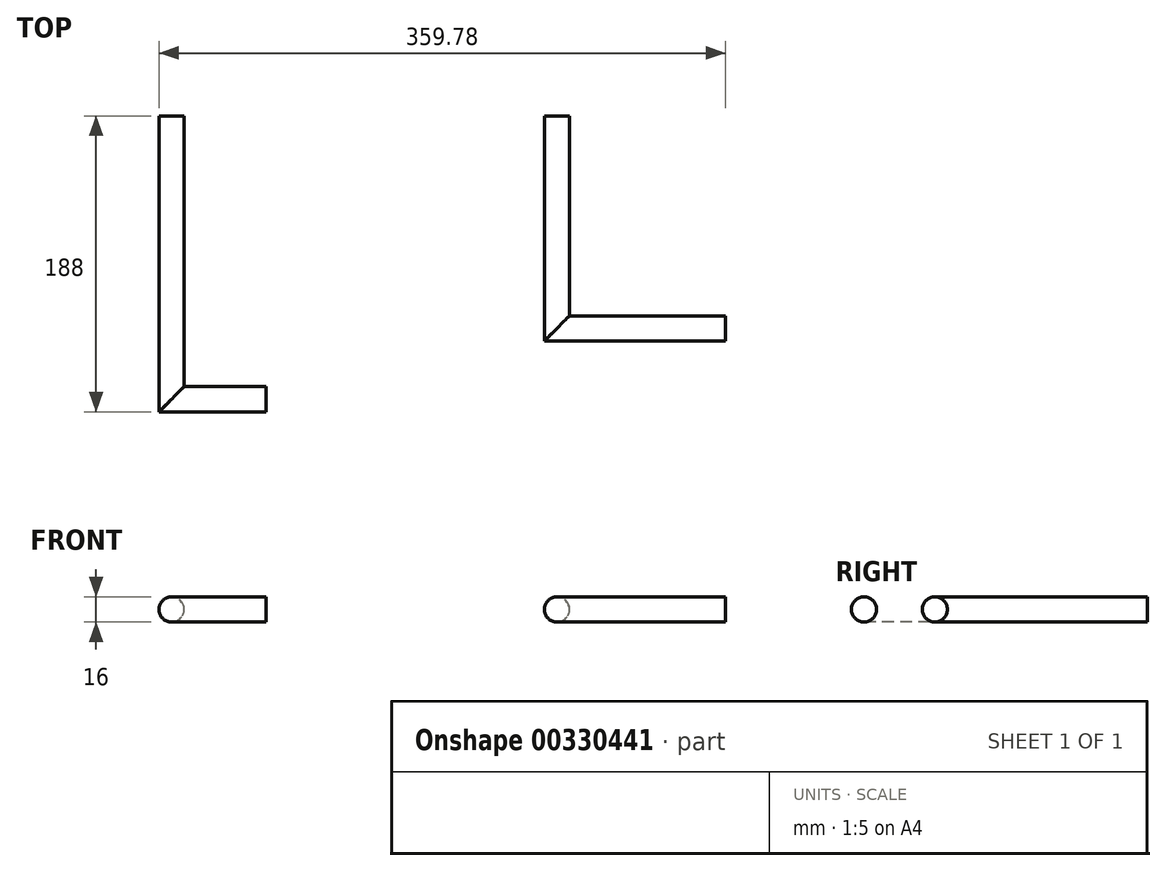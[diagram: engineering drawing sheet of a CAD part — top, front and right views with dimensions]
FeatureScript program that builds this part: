
annotation { "Feature Type Name" : "Feature", "Feature Type Description" : "" }
export const myFeature = defineFeature(function(context is Context, id is Id, definition is map)
    precondition{}
    {
        {
            var Q0;
            Q0=qCreatedBy(makeId("Top.planeOp"),FACE);
            var sketch = newSketch(context, id + "F0", { "sketchPlane" : qUnion([Q0])});
            skLineSegment(sketch, "E0", {"start": v(0, 0) * mm, "end": v(0, -135) * mm});
            skLineSegment(sketch, "E1", {"start": v(0, -135) * mm, "end": v(107, -135) * mm});
            skSolve(sketch);
        }
        {
            var Q0;
            Q0=qCreatedBy(makeId("Front.planeOp"),FACE);
            var sketch = newSketch(context, id + "F1", { "sketchPlane" : qUnion([Q0])});
            skCircle(sketch, "E2", {"center": v(0, 0) * mm, "radius": 8 * mm});
            skSolve(sketch);
        }
        {
            var Q0;
            Q0=makeQuery(id+"F1.imprint","IMPRINT",FACE,{"disambiguationData":[TD([[makeQuery(id+"F1.imprint","IMPRINT",EDGE,{"derivedFrom":sQuery(id+"F1.wireOp",EDGE,"E2")}),1.0]])]});
            var Q1;
            Q1=sQuery(id+"F0.wireOp",EDGE,"E0");
            var Q2;
            Q2=sQuery(id+"F0.wireOp",EDGE,"E1");
            sweep(context, id + "F2", {"profiles" : qUnion([Q0]), "path" : qUnion([Q1, Q2])});
        }
        {
            var Q0;
            Q0=qCreatedBy(makeId("Top.planeOp"),FACE);
            var sketch = newSketch(context, id + "F3", { "sketchPlane" : qUnion([Q0])});
            skLineSegment(sketch, "E3", {"start": v(-244.78, 0) * mm, "end": v(-244.78, -180) * mm});
            skLineSegment(sketch, "E4", {"start": v(-244.78, -180) * mm, "end": v(-184.78, -180) * mm});
            skSolve(sketch);
        }
        {
            var Q0;
            Q0=qCreatedBy(makeId("Front.planeOp"),FACE);
            var sketch = newSketch(context, id + "F4", { "sketchPlane" : qUnion([Q0])});
            skPoint(sketch, "E5.0", {"position": v(-244.78, 0) * mm});
            skCircle(sketch, "E6", {"center": v(-244.78, 0) * mm, "radius": 8 * mm});
            skSolve(sketch);
        }
        {
            var Q0;
            Q0=makeQuery(id+"F4.imprint","IMPRINT",FACE,{"disambiguationData":[TD([[makeQuery(id+"F4.imprint","IMPRINT",EDGE,{"derivedFrom":sQuery(id+"F4.wireOp",EDGE,"E6")}),1.0]])]});
            var Q1;
            Q1=sQuery(id+"F3.wireOp",EDGE,"E3");
            var Q2;
            Q2=sQuery(id+"F3.wireOp",EDGE,"E4");
            sweep(context, id + "F5", {"profiles" : qUnion([Q0]), "path" : qUnion([Q1, Q2])});
        }
    });
